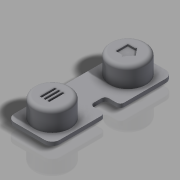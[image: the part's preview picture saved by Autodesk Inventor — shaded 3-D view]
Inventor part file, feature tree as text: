
AUTODESK INVENTOR PART (.ipt)
format: ipt  version: 2019 (Build 230136000, 136)  size: 276,992 bytes
history: native  units: in
note: dims shown in document units (in); Inventor stores cm internally (conversion verified against a paired STEP export)
features: extrude x8, sketch x5, fillet x3
ambient origin geometry x8: Origin, YZ Plane, XZ Plane, XY Plane, X Axis, Y Axis, Z Axis, Center Point
bodies: Solid1 (feature_tree)
feature tree (16):
  sketch  "Sketch1"  dims[d0=0.2362in d1=0.6299in]
  extrude  "Extrusion1"  Depth=0.6299in
  extrude  "Extrusion2"  Depth=0.189in
  fillet  "Fillet1"  Radius=0.1181in
  sketch  "Sketch2"  dims[d2=0.189in d3=0.189in d5=0.1181in]
  extrude  "Extrusion3"  Depth=0.0787in
  extrude  "Extrusion4"  Depth=0.0787in
  sketch  "Sketch4"  dims[d6=0.0394in d7=0.0787in]
  extrude  "Extrusion5"  Depth=0.1043in TaperAngle=0.0deg
  extrude  "Extrusion6"  Depth=0.0197in
  sketch  "Sketch6"  dims[d11=0.0197in d12=0.0in d13=0.1043in d14=0.0in d15=0.0197in d18=0.1181in d19=0.1181in d20=0.0787in d21=0.0in d22=0.1575in d23=0.1575in d24=0.0295in d25=0.0in d26=0.0236in d27=0.1378in d28=0.0236in d29=0.1378in d30=0.0787in d31=0.0in d32=0.0472in d33=0.0472in d34=0.0236in d35=0.0236in d36=0.0295in d37=0.0in d40=0.2749in d41=0.6871in d43=0.063in d44=0.0394in d45=0.0098in d46=0.0in d47=0.0098in d48=0.0787in d50=0.0394in d52=1.1811in d54=0.0197in d55=0.3937in d57=0.3937in d59=0.0246in d60=0.0098in d61=0.0in d62=0.0315in d63=0.002in d66=0.002in d69=0.0315in d70=0.0787in d71=0.0787in d72=0.0197in d73=0.0197in d74=0.0in]
  extrude  "Extrusion7"  Depth=0.1181in
  extrude  "Extrusion8"  Depth=0.1181in
  fillet  "Fillet6"  Radius=0.0787in
  fillet  "Fillet9"  Radius=0.1575in
  sketch  "Sketch5"  dims[d8=0.1575in d9=0.0787in]
